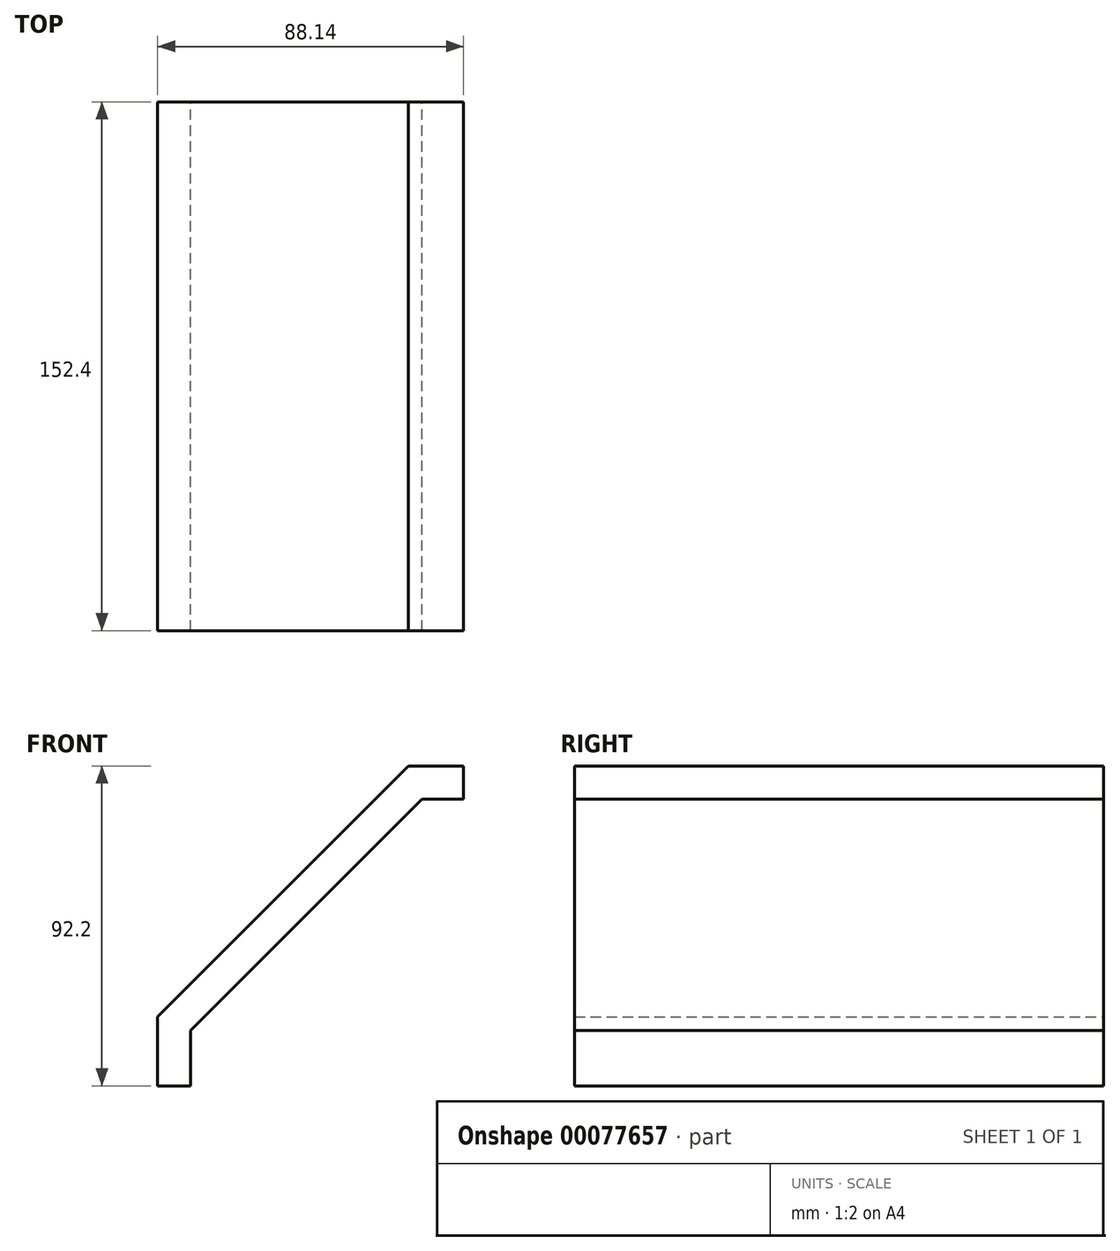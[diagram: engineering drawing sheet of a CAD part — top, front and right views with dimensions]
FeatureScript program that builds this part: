
annotation { "Feature Type Name" : "Feature", "Feature Type Description" : "" }
export const myFeature = defineFeature(function(context is Context, id is Id, definition is map)
    precondition{}
    {
        {
            var Q0;
            Q0=qCreatedBy(makeId("Front.planeOp"),FACE);
            var sketch = newSketch(context, id + "F0", { "sketchPlane" : qUnion([Q0])});
            skLineSegment(sketch, "E0", {"start": v(-44.07, -46.1) * mm, "end": v(-44.07, -26.27) * mm});
            skLineSegment(sketch, "E1", {"start": v(-44.07, -26.27) * mm, "end": v(28.2, 46.1) * mm});
            skLineSegment(sketch, "E2", {"start": v(-34.54, -30.2) * mm, "end": v(32.14, 36.58) * mm});
            skLineSegment(sketch, "E3", {"start": v(-44.07, -46.1) * mm, "end": v(-34.54, -46.1) * mm});
            skLineSegment(sketch, "E4", {"start": v(44.07, 46.1) * mm, "end": v(44.07, 36.58) * mm});
            skLineSegment(sketch, "E5", {"start": v(-34.54, -46.1) * mm, "end": v(-34.54, -30.2) * mm});
            skLineSegment(sketch, "E6", {"start": v(44.07, 36.58) * mm, "end": v(32.14, 36.58) * mm});
            skLineSegment(sketch, "E7", {"start": v(28.2, 46.1) * mm, "end": v(44.07, 46.1) * mm});
            skSolve(sketch);
        }
        {
            var Q0;
            Q0=makeQuery(id+"F0.imprint","IMPRINT",FACE,{"disambiguationData":[TD([[makeQuery(id+"F0.imprint","IMPRINT",EDGE,{"derivedFrom":sQuery(id+"F0.wireOp",EDGE,"E0")}),-1.0]])]});
            extrude(context, id + "F1", {"entities" : qUnion([Q0]), "depth" : 152.4 * mm});
        }
    });
